# Revit family: Detail-Shades-Hunter_Douglas-RB500-Heavy_Duty-Auto-Bracket-75L-Pocket_Details
name_source: partatom
category: Detail Items
units: mm (PartAtom-declared; Revit-internal decimal feet)

## family parameters
OmniClass Number = 23.30.60.14
OmniClass Title = Interior Window Treatment
Rotate with component = No
Section Shape = Not Defined
Shared = No

## types (1)
- Gypsum Pocket
    Assembly Code = E2010300
    CD_Height = 6"
    CD_Install Documentation = https://www.hunterdouglasarchitectural.com
    CD_Microsite = https://microsite.caddetails.com
    CD_Product Documentation Link = https://www.hunterdouglasarchitectural.com
    CD_Product Name = RB 500 Roller Shade System
    CD_Product Page URL = https://www.hunterdouglasarchitectural.com
    CD_Warranty = https://assets.hunterdouglasarchitectural.com
    CD_Width = 6"
    Description = Heavy Duty Automatic Roller Shade
    Manufacturer = Hunter Douglas Architectural
    Model = Heavy Duty Automatic 75L Bracket
    Type Comments = Gypsum Pocket
    URL = https://www.hunterdouglasarchitectural.com

## geometry (parser evidence)
native form markers: Sweep x1
no freeform markers — native parametric forms only
